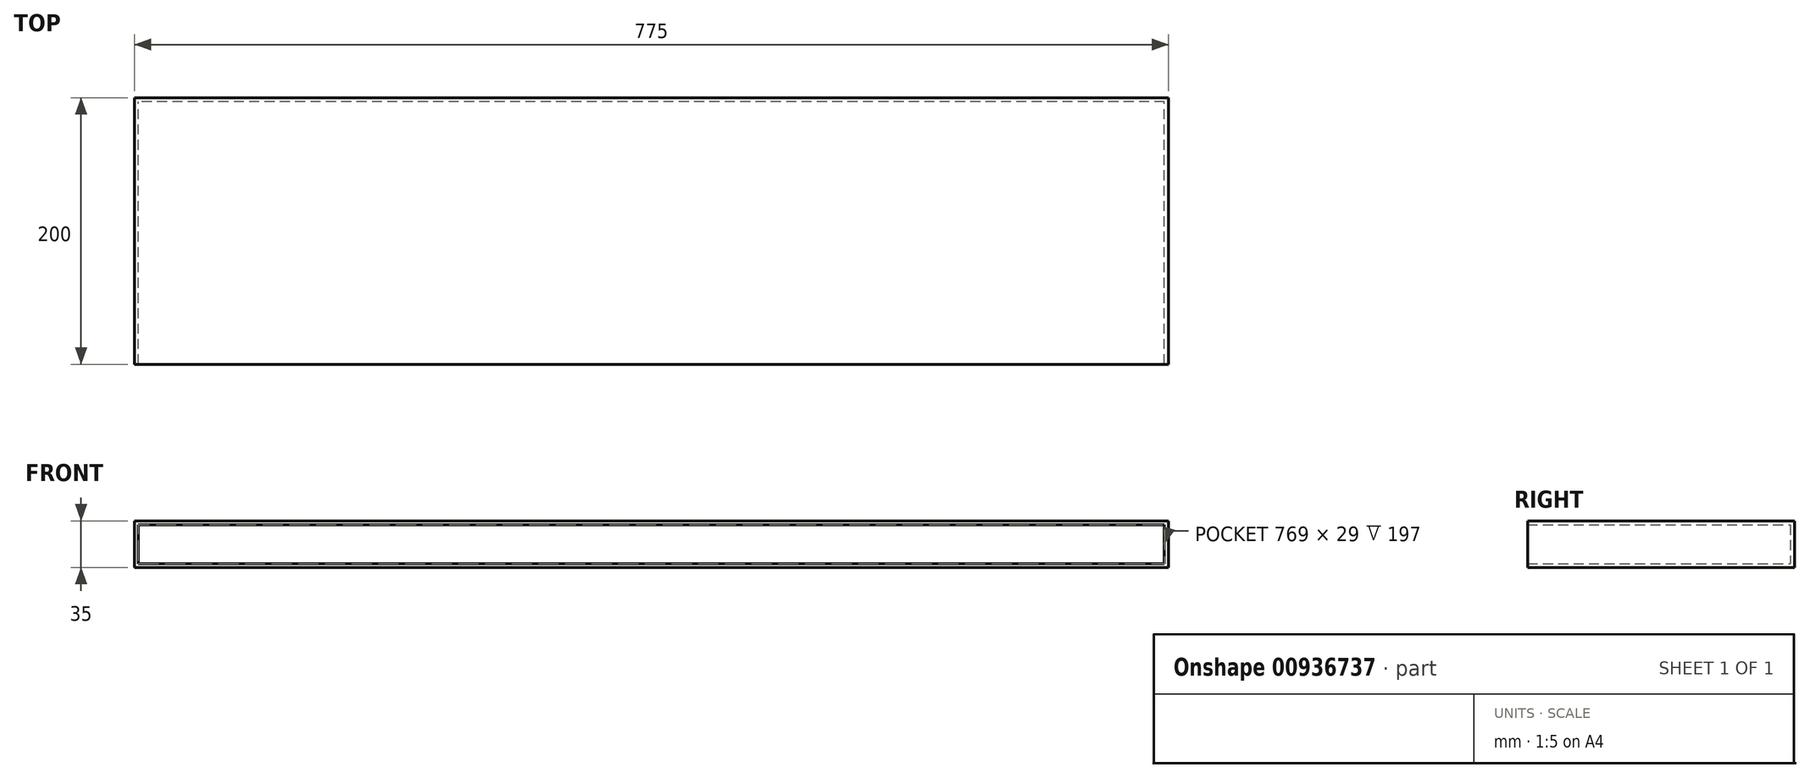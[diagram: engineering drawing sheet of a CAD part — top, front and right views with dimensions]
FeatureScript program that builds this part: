
annotation { "Feature Type Name" : "Feature", "Feature Type Description" : "" }
export const myFeature = defineFeature(function(context is Context, id is Id, definition is map)
    precondition{}
    {
        {
            var Q0;
            Q0=qCreatedBy(makeId("Top.planeOp"),FACE);
            var sketch = newSketch(context, id + "F0", { "sketchPlane" : qUnion([Q0])});
            skLineSegment(sketch, "E0.bottom", {"start": v(387.5, -100) * mm, "end": v(-387.5, -100) * mm});
            skLineSegment(sketch, "E0.top", {"start": v(387.5, 100) * mm, "end": v(-387.5, 100) * mm});
            skLineSegment(sketch, "E0.left", {"start": v(387.5, -100) * mm, "end": v(387.5, 100) * mm});
            skLineSegment(sketch, "E0.right", {"start": v(-387.5, -100) * mm, "end": v(-387.5, 100) * mm});
            skPoint(sketch, "E0.middle", {"position": v(0, 0) * mm});
            skSolve(sketch);
        }
        {
            var Q0;
            Q0=makeQuery(id+"F0.imprint","IMPRINT",FACE,{"disambiguationData":[TD([[makeQuery(id+"F0.imprint","IMPRINT",EDGE,{"derivedFrom":sQuery(id+"F0.wireOp",EDGE,"E0.bottom")}),-1.0]])]});
            extrude(context, id + "F1", {"entities" : qUnion([Q0]), "depth" : 35 * mm, "offsetDistance" : 25 * mm});
        }
        {
            var Q0;
            Q0=makeQuery(id+"F1.opExtrude","SWEPT_FACE",FACE,{"disambiguationData":[OSD([sQuery(id+"F0.wireOp",EDGE,"E0.bottom")])]});
            shell(context, id + "F2", {"entities" : qUnion([Q0]), "thickness" : 3 * mm});
        }
    });
